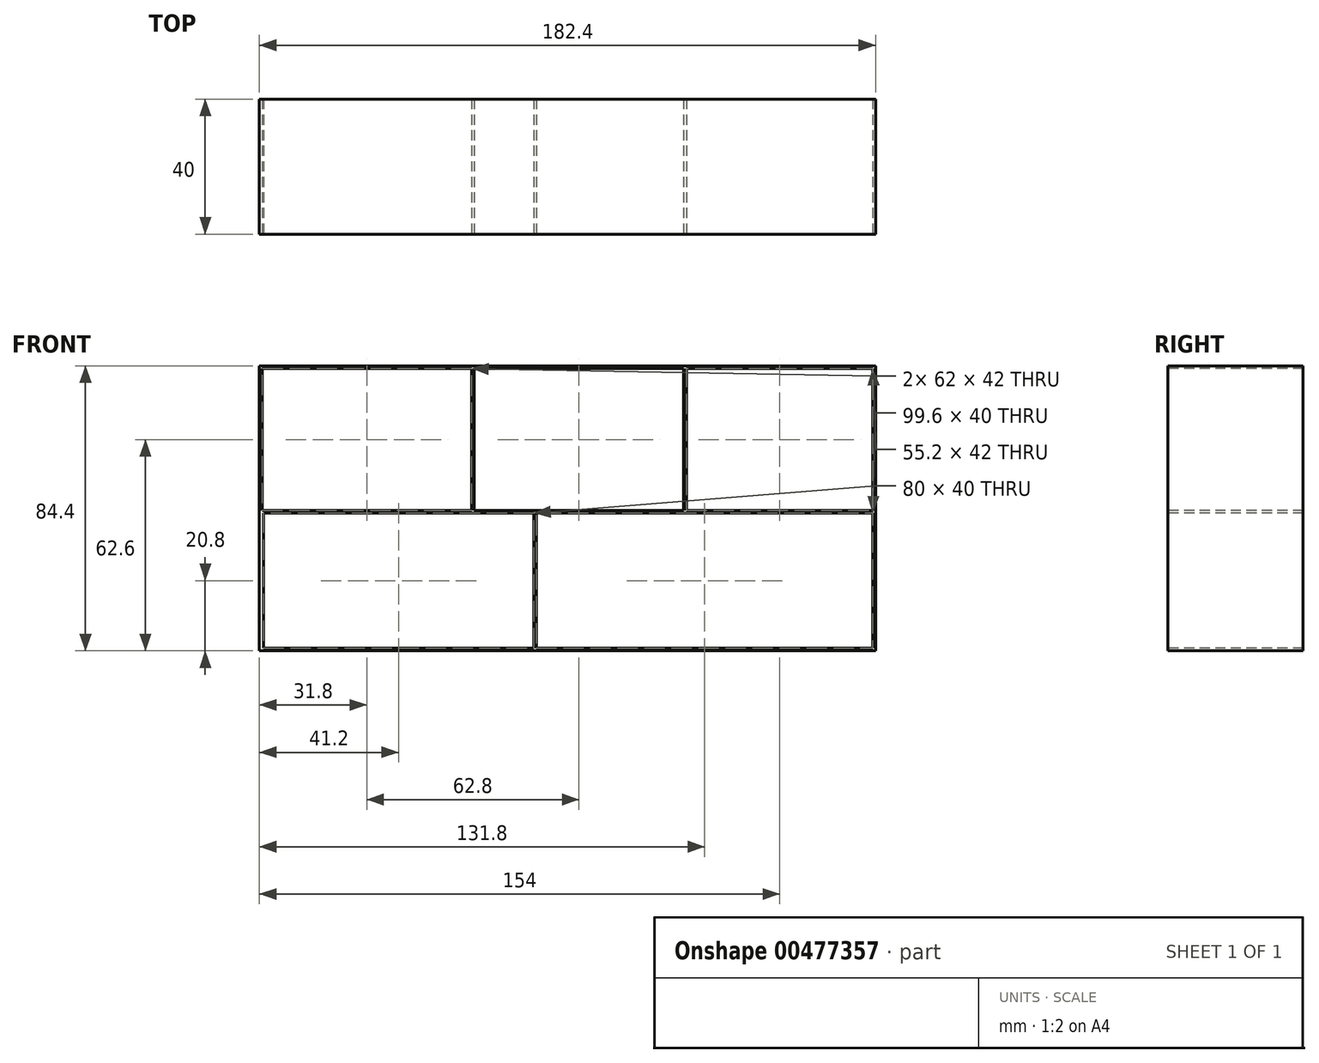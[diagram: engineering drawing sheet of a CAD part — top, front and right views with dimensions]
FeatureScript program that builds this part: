
annotation { "Feature Type Name" : "Feature", "Feature Type Description" : "" }
export const myFeature = defineFeature(function(context is Context, id is Id, definition is map)
    precondition{}
    {
        {
            var Q0;
            Q0=qCreatedBy(makeId("Top.planeOp"),FACE);
            var sketch = newSketch(context, id + "F0", { "sketchPlane" : qUnion([Q0])});
            skLineSegment(sketch, "E0.bottom", {"start": v(-91.2, 20) * mm, "end": v(91.2, 20) * mm});
            skLineSegment(sketch, "E0.top", {"start": v(-91.2, -20) * mm, "end": v(91.2, -20) * mm});
            skLineSegment(sketch, "E0.left", {"start": v(-91.2, 20) * mm, "end": v(-91.2, -20) * mm});
            skLineSegment(sketch, "E0.right", {"start": v(91.2, 20) * mm, "end": v(91.2, -20) * mm});
            skPoint(sketch, "E0.middle", {"position": v(0, 0) * mm});
            skSolve(sketch);
        }
        {
            var Q0;
            Q0=makeQuery(id+"F0.imprint","IMPRINT",FACE,{"disambiguationData":[TD([[makeQuery(id+"F0.imprint","IMPRINT",EDGE,{"derivedFrom":sQuery(id+"F0.wireOp",EDGE,"E0.bottom")}),-1.0]])]});
            extrude(context, id + "F1", {"entities" : qUnion([Q0]), "depth" : 84.4 * mm});
        }
        {
            var Q0;
            Q0=makeQuery(id+"F1.opExtrude","SWEPT_FACE",FACE,{"disambiguationData":[OSD([sQuery(id+"F0.wireOp",EDGE,"E0.top")])]});
            var sketch = newSketch(context, id + "F2", { "sketchPlane" : qUnion([Q0])});
            skLineSegment(sketch, "E1.bottom", {"start": v(-90, 40.8) * mm, "end": v(90.4, 40.8) * mm});
            skLineSegment(sketch, "E1.top", {"start": v(-90, 0.8) * mm, "end": v(90.4, 0.8) * mm});
            skLineSegment(sketch, "E1.left", {"start": v(-90, 40.8) * mm, "end": v(-90, 0.8) * mm});
            skLineSegment(sketch, "E1.right", {"start": v(90.4, 40.8) * mm, "end": v(90.4, 0.8) * mm});
            skLineSegment(sketch, "E2.0", {"start": v(-91.2, 84.4) * mm, "end": v(-91.2, 0) * mm});
            skLineSegment(sketch, "E3.0", {"start": v(91.2, 84.4) * mm, "end": v(91.2, 0) * mm});
            skLineSegment(sketch, "E4.0", {"start": v(-91.2, 84.4) * mm, "end": v(91.2, 84.4) * mm});
            skLineSegment(sketch, "E5.0", {"start": v(-91.2, 0) * mm, "end": v(91.2, 0) * mm});
            skLineSegment(sketch, "E6.0", {"start": v(-9.2, 40.8) * mm, "end": v(-9.2, 0.8) * mm});
            skLineSegment(sketch, "E7.0", {"start": v(-10, 40.8) * mm, "end": v(-10, 0.8) * mm});
            skLineSegment(sketch, "E8.bottom", {"start": v(-90.4, 83.6) * mm, "end": v(90.4, 83.6) * mm});
            skLineSegment(sketch, "E8.top", {"start": v(-90.4, 41.6) * mm, "end": v(90.4, 41.6) * mm});
            skLineSegment(sketch, "E8.left", {"start": v(-90.4, 83.6) * mm, "end": v(-90.4, 41.6) * mm});
            skLineSegment(sketch, "E8.right", {"start": v(90.4, 83.6) * mm, "end": v(90.4, 41.6) * mm});
            skLineSegment(sketch, "E9.0", {"start": v(-28.4, 83.6) * mm, "end": v(-28.4, 41.6) * mm});
            skLineSegment(sketch, "E10.0", {"start": v(-27.6, 83.6) * mm, "end": v(-27.6, 41.6) * mm});
            skLineSegment(sketch, "E11.0", {"start": v(34.4, 83.6) * mm, "end": v(34.4, 41.6) * mm});
            skLineSegment(sketch, "E12.0", {"start": v(-91.2, 84.15) * mm, "end": v(91.2, 84.15) * mm});
            skLineSegment(sketch, "E13.0", {"start": v(35.2, 83.6) * mm, "end": v(35.2, 41.6) * mm});
            skSolve(sketch);
        }
        {
            var Q0;
            {var subQ0=sQuery(id+"F2.wireOp",EDGE,"E1.right");Q0=makeQuery(id+"F2.imprint","IMPRINT",FACE,{"disambiguationData":[TD([[makeQuery(id+"F2.imprint","IMPRINT",EDGE,{"derivedFrom":subQ0}),-1.0]])]});}
            var Q1;
            {var subQ0=sQuery(id+"F2.wireOp",EDGE,"E1.left");Q1=makeQuery(id+"F2.imprint","IMPRINT",FACE,{"disambiguationData":[TD([[makeQuery(id+"F2.imprint","IMPRINT",EDGE,{"derivedFrom":subQ0}),1.0]])]});}
            var Q2;
            {var subQ0=sQuery(id+"F2.wireOp",EDGE,"E8.right");Q2=makeQuery(id+"F2.imprint","IMPRINT",FACE,{"disambiguationData":[TD([[makeQuery(id+"F2.imprint","IMPRINT",EDGE,{"derivedFrom":subQ0}),-1.0]])]});}
            var Q3;
            {var subQ0=sQuery(id+"F2.wireOp",EDGE,"E8.left");Q3=makeQuery(id+"F2.imprint","IMPRINT",FACE,{"disambiguationData":[TD([[makeQuery(id+"F2.imprint","IMPRINT",EDGE,{"derivedFrom":subQ0}),1.0]])]});}
            var Q4;
            {var subQ0=sQuery(id+"F2.wireOp",EDGE,"E10.0");Q4=makeQuery(id+"F2.imprint","IMPRINT",FACE,{"disambiguationData":[TD([[makeQuery(id+"F2.imprint","IMPRINT",EDGE,{"derivedFrom":subQ0}),1.0]])]});}
            extrude(context, id + "F3", {"entities" : qUnion([Q0, Q1, Q2, Q3, Q4]), "operationType" : NewBodyOperationType.REMOVE, "oppositeDirection" : true, "depth" : 833.7 * mm});
        }
    });
